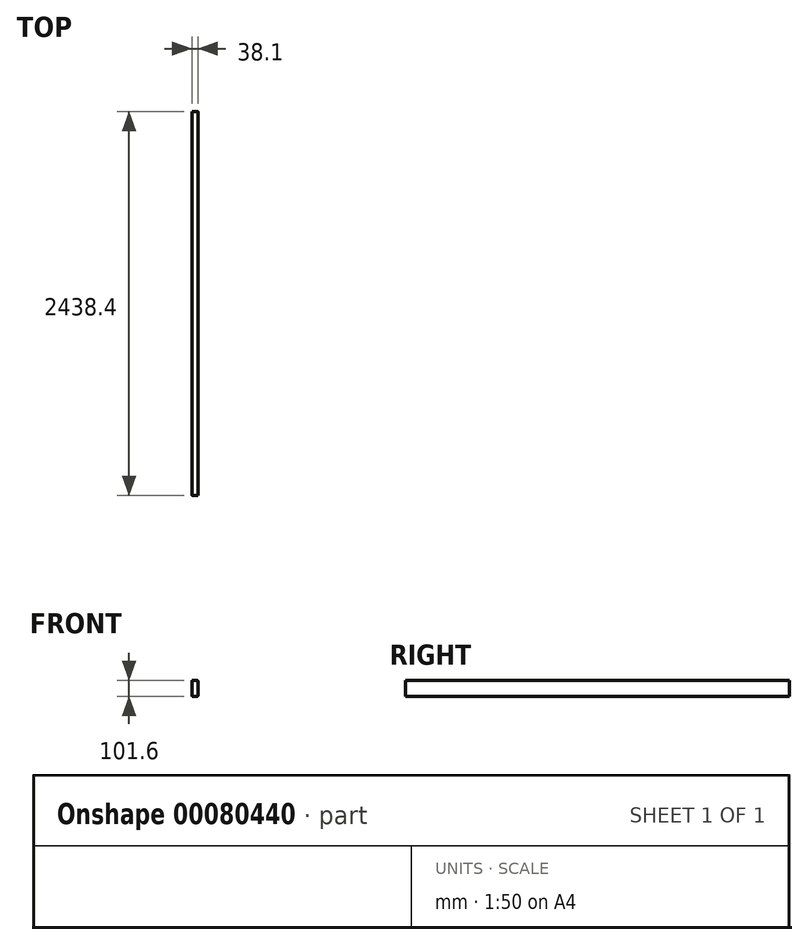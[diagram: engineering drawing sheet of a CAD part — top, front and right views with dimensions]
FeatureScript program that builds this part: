
annotation { "Feature Type Name" : "Feature", "Feature Type Description" : "" }
export const myFeature = defineFeature(function(context is Context, id is Id, definition is map)
    precondition{}
    {
        {
            var Q0;
            Q0=qCreatedBy(makeId("Front.planeOp"),FACE);
            var sketch = newSketch(context, id + "F0", { "sketchPlane" : qUnion([Q0])});
            skLineSegment(sketch, "E0.bottom", {"start": v(-27.1, 43.3) * mm, "end": v(1.47, 43.3) * mm});
            skLineSegment(sketch, "E0.top", {"start": v(-27.1, -58.3) * mm, "end": v(1.47, -58.3) * mm});
            skLineSegment(sketch, "E0.left", {"start": v(-31.86, 38.54) * mm, "end": v(-31.86, -53.53) * mm});
            skLineSegment(sketch, "E0.right", {"start": v(6.24, 38.54) * mm, "end": v(6.24, -53.53) * mm});
            skPoint(sketch, "E1.visualSharp", {"position": v(-31.86, 43.3) * mm});
            skArc(sketch, "E1.filletArc", {"start": v(-27.1, 43.3) * mm, "mid": v(-30.47, 41.9) * mm, "end": v(-31.86, 38.54) * mm});
            skPoint(sketch, "E2.visualSharp", {"position": v(6.24, 43.3) * mm});
            skArc(sketch, "E2.filletArc", {"start": v(6.24, 38.54) * mm, "mid": v(4.84, 41.9) * mm, "end": v(1.47, 43.3) * mm});
            skPoint(sketch, "E3.visualSharp", {"position": v(6.24, -58.3) * mm});
            skArc(sketch, "E3.filletArc", {"start": v(1.47, -58.3) * mm, "mid": v(4.84, -56.9) * mm, "end": v(6.24, -53.53) * mm});
            skPoint(sketch, "E4.visualSharp", {"position": v(-31.86, -58.3) * mm});
            skArc(sketch, "E4.filletArc", {"start": v(-31.86, -53.53) * mm, "mid": v(-30.47, -56.9) * mm, "end": v(-27.1, -58.3) * mm});
            skSolve(sketch);
        }
        {
            var Q0;
            Q0 = qSketchRegion(id + "F0", true);
            extrude(context, id + "F1", {"entities" : qUnion([Q0]), "depth" : 2438.4 * mm});
        }
    });
